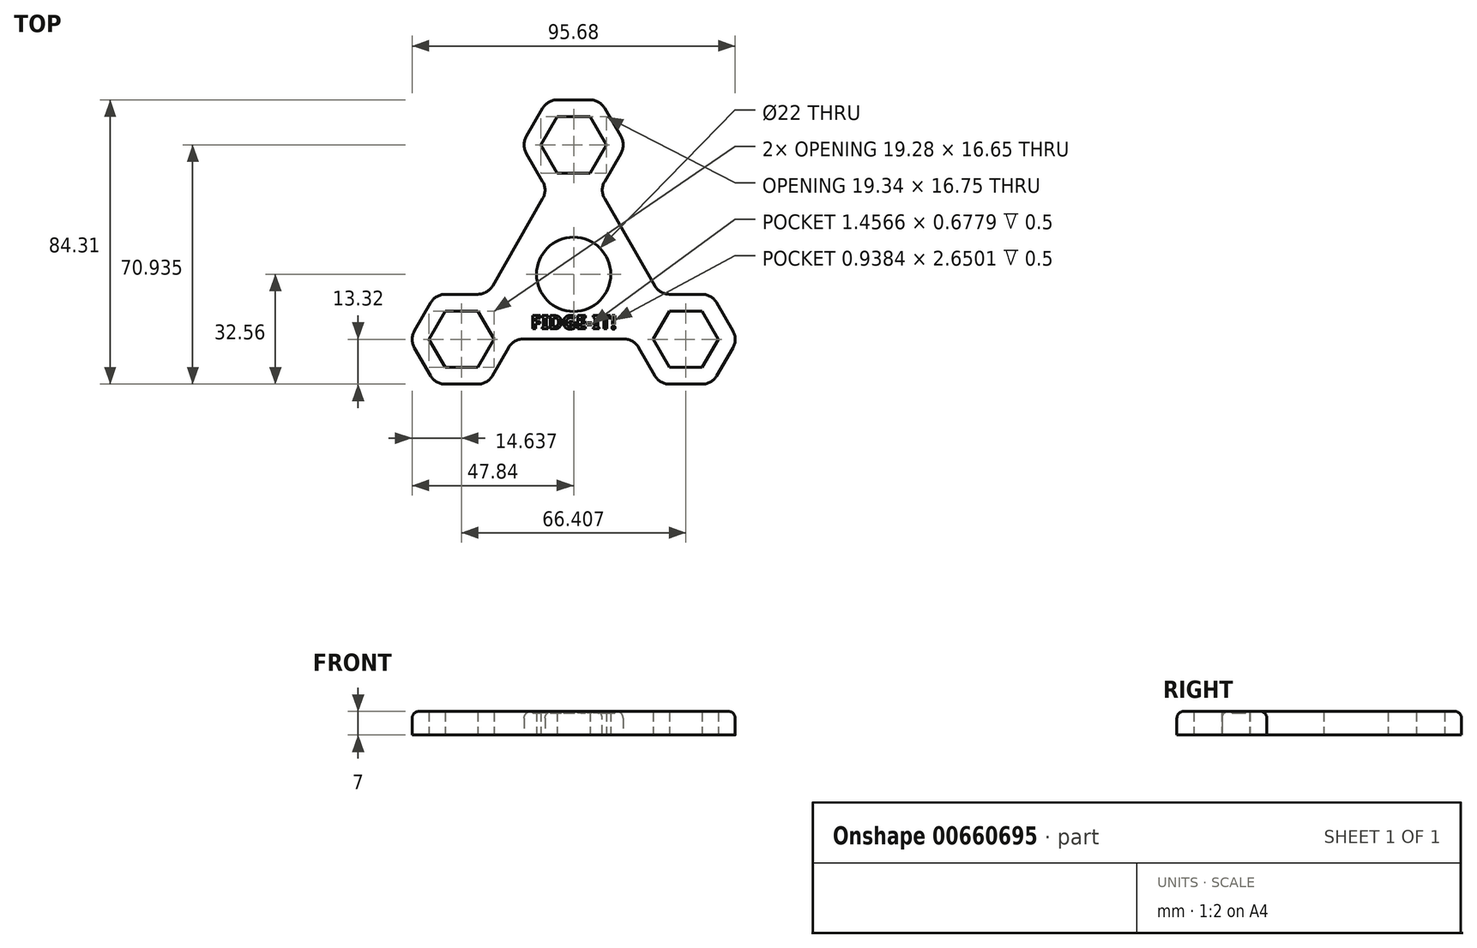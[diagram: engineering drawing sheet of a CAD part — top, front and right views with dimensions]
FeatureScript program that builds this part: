
annotation { "Feature Type Name" : "Feature", "Feature Type Description" : "" }
export const myFeature = defineFeature(function(context is Context, id is Id, definition is map)
    precondition{}
    {
        {
            var Q0;
            Q0=qCreatedBy(makeId("Top.planeOp"),FACE);
            var sketch = newSketch(context, id + "F0", { "sketchPlane" : qUnion([Q0])});
            skCircle(sketch, "E0", {"center": v(0, 0) * mm, "radius": 11 * mm});
            skLineSegment(sketch, "E1.0", {"start": v(4.84, 30) * mm, "end": v(-4.84, 30) * mm});
            skLineSegment(sketch, "E1.1", {"start": v(-4.84, 30) * mm, "end": v(-9.67, 38.38) * mm});
            skLineSegment(sketch, "E1.2", {"start": v(-9.67, 38.38) * mm, "end": v(-4.84, 46.75) * mm});
            skLineSegment(sketch, "E1.3", {"start": v(-4.84, 46.75) * mm, "end": v(4.84, 46.75) * mm});
            skLineSegment(sketch, "E1.4", {"start": v(4.84, 46.75) * mm, "end": v(9.67, 38.37) * mm});
            skLineSegment(sketch, "E1.5", {"start": v(9.67, 38.37) * mm, "end": v(4.84, 30) * mm});
            skPoint(sketch, "E1.0.midPoint", {"position": v(0, 30) * mm});
            skLineSegment(sketch, "E2.2.0", {"start": v(42.84, -19.3) * mm, "end": v(38.07, -27.56) * mm});
            skLineSegment(sketch, "E2.2.1", {"start": v(28.4, -27.56) * mm, "end": v(23.56, -19.19) * mm});
            skLineSegment(sketch, "E2.2.2", {"start": v(38.07, -27.56) * mm, "end": v(28.4, -27.56) * mm});
            skLineSegment(sketch, "E2.2.3", {"start": v(38, -10.92) * mm, "end": v(42.84, -19.3) * mm});
            skPoint(sketch, "E2.2.5", {"position": v(25.98, -15) * mm});
            skLineSegment(sketch, "E2.2.6", {"start": v(28.34, -10.92) * mm, "end": v(38, -10.92) * mm});
            skLineSegment(sketch, "E2.2.7", {"start": v(23.56, -19.19) * mm, "end": v(28.34, -10.92) * mm});
            skPoint(sketch, "E1.cCircle.center.orphan", {"position": v(0, 38.38) * mm});
            skLineSegment(sketch, "E3.0", {"start": v(-7.72, 25) * mm, "end": v(-15.44, 38.38) * mm});
            skLineSegment(sketch, "E3.1", {"start": v(-7.72, 51.75) * mm, "end": v(7.72, 51.75) * mm});
            skLineSegment(sketch, "E3.2", {"start": v(7.72, 51.75) * mm, "end": v(15.44, 38.37) * mm});
            skLineSegment(sketch, "E3.3", {"start": v(-15.44, 38.38) * mm, "end": v(-7.72, 51.75) * mm});
            skLineSegment(sketch, "E3.4", {"start": v(15.44, 38.37) * mm, "end": v(7.72, 25) * mm});
            skLineSegment(sketch, "E4.0", {"start": v(25.51, -32.56) * mm, "end": v(17.79, -19.19) * mm});
            skLineSegment(sketch, "E4.1", {"start": v(25.45, -5.92) * mm, "end": v(40.9, -5.92) * mm});
            skLineSegment(sketch, "E4.2", {"start": v(40.9, -5.92) * mm, "end": v(48.62, -19.3) * mm});
            skLineSegment(sketch, "E4.4", {"start": v(48.62, -19.3) * mm, "end": v(40.96, -32.56) * mm});
            skLineSegment(sketch, "E4.5", {"start": v(40.96, -32.56) * mm, "end": v(25.51, -32.56) * mm});
            skLineSegment(sketch, "E5.MirrorCS", {"start": v(-23.56, -19.19) * mm, "end": v(-28.34, -10.92) * mm});
            skPoint(sketch, "E6.MirrorP", {"position": v(-25.98, -15) * mm});
            skLineSegment(sketch, "E7.MirrorCS", {"start": v(-28.34, -10.92) * mm, "end": v(-38, -10.92) * mm});
            skLineSegment(sketch, "E8.MirrorCS", {"start": v(-40.96, -32.56) * mm, "end": v(-25.51, -32.56) * mm});
            skLineSegment(sketch, "E9.MirrorCS", {"start": v(-42.84, -19.3) * mm, "end": v(-38.07, -27.56) * mm});
            skLineSegment(sketch, "E10.MirrorCS", {"start": v(-38, -10.92) * mm, "end": v(-42.84, -19.3) * mm});
            skLineSegment(sketch, "E11.MirrorCS", {"start": v(-25.51, -32.56) * mm, "end": v(-17.79, -19.19) * mm});
            skLineSegment(sketch, "E12.MirrorCS", {"start": v(-48.62, -19.3) * mm, "end": v(-40.96, -32.56) * mm});
            skLineSegment(sketch, "E13.MirrorCS", {"start": v(-40.9, -5.92) * mm, "end": v(-48.62, -19.3) * mm});
            skLineSegment(sketch, "E14.MirrorCS", {"start": v(-28.4, -27.56) * mm, "end": v(-23.56, -19.19) * mm});
            skLineSegment(sketch, "E15.MirrorCS", {"start": v(-38.07, -27.56) * mm, "end": v(-28.4, -27.56) * mm});
            skLineSegment(sketch, "E16.MirrorCS", {"start": v(-25.45, -5.92) * mm, "end": v(-40.9, -5.92) * mm});
            skLineSegment(sketch, "E17", {"start": v(-7.72, 25) * mm, "end": v(-25.45, -5.92) * mm});
            skLineSegment(sketch, "E18", {"start": v(7.72, 25) * mm, "end": v(25.45, -5.92) * mm});
            skLineSegment(sketch, "E19", {"start": v(17.79, -19.19) * mm, "end": v(-17.79, -19.19) * mm});
            skSolve(sketch);
        }
        {
            var Q0;
            Q0=makeQuery(id+"F0.imprint","IMPRINT",FACE,{"disambiguationData":[TD([[makeQuery(id+"F0.imprint","IMPRINT",EDGE,{"derivedFrom":sQuery(id+"F0.wireOp",EDGE,"E1.0")}),1.0]])]});
            extrude(context, id + "F1", {"entities" : qUnion([Q0]), "depth" : 7 * mm, "offsetDistance" : 25 * mm});
        }
        {
            var Q0;
            Q0=makeQuery(id+"F1.opExtrude","SWEPT_EDGE",EDGE,{"disambiguationData":[OSD([sQuery(id+"F0.wireOp",EDGE,"E8.MirrorCS"),sQuery(id+"F0.wireOp",EDGE,"E11.MirrorCS")])]});
            var Q1;
            Q1=makeQuery(id+"F1.opExtrude","SWEPT_EDGE",EDGE,{"disambiguationData":[OSD([sQuery(id+"F0.wireOp",EDGE,"E8.MirrorCS"),sQuery(id+"F0.wireOp",EDGE,"E12.MirrorCS")])]});
            var Q2;
            Q2=makeQuery(id+"F1.opExtrude","SWEPT_EDGE",EDGE,{"disambiguationData":[OSD([sQuery(id+"F0.wireOp",EDGE,"E12.MirrorCS"),sQuery(id+"F0.wireOp",EDGE,"E13.MirrorCS")])]});
            var Q3;
            Q3=makeQuery(id+"F1.opExtrude","SWEPT_EDGE",EDGE,{"disambiguationData":[OSD([sQuery(id+"F0.wireOp",EDGE,"E13.MirrorCS"),sQuery(id+"F0.wireOp",EDGE,"E16.MirrorCS")])]});
            var Q4;
            Q4=makeQuery(id+"F1.opExtrude","SWEPT_EDGE",EDGE,{"disambiguationData":[OSD([sQuery(id+"F0.wireOp",EDGE,"E16.MirrorCS"),sQuery(id+"F0.wireOp",EDGE,"E17")])]});
            var Q5;
            Q5=makeQuery(id+"F1.opExtrude","SWEPT_EDGE",EDGE,{"disambiguationData":[OSD([sQuery(id+"F0.wireOp",EDGE,"E11.MirrorCS"),sQuery(id+"F0.wireOp",EDGE,"E19")])]});
            var Q6;
            Q6=makeQuery(id+"F1.opExtrude","SWEPT_EDGE",EDGE,{"disambiguationData":[OSD([sQuery(id+"F0.wireOp",EDGE,"E4.0"),sQuery(id+"F0.wireOp",EDGE,"E19")])]});
            var Q7;
            Q7=makeQuery(id+"F1.opExtrude","SWEPT_EDGE",EDGE,{"disambiguationData":[OSD([sQuery(id+"F0.wireOp",EDGE,"E4.0"),sQuery(id+"F0.wireOp",EDGE,"E4.5")])]});
            var Q8;
            Q8=makeQuery(id+"F1.opExtrude","SWEPT_EDGE",EDGE,{"disambiguationData":[OSD([sQuery(id+"F0.wireOp",EDGE,"E4.4"),sQuery(id+"F0.wireOp",EDGE,"E4.5")])]});
            var Q9;
            Q9=makeQuery(id+"F1.opExtrude","SWEPT_EDGE",EDGE,{"disambiguationData":[OSD([sQuery(id+"F0.wireOp",EDGE,"E4.2"),sQuery(id+"F0.wireOp",EDGE,"E4.4")])]});
            var Q10;
            Q10=makeQuery(id+"F1.opExtrude","SWEPT_EDGE",EDGE,{"disambiguationData":[OSD([sQuery(id+"F0.wireOp",EDGE,"E4.1"),sQuery(id+"F0.wireOp",EDGE,"E4.2")])]});
            var Q11;
            Q11=makeQuery(id+"F1.opExtrude","SWEPT_EDGE",EDGE,{"disambiguationData":[OSD([sQuery(id+"F0.wireOp",EDGE,"E4.1"),sQuery(id+"F0.wireOp",EDGE,"E18")])]});
            var Q12;
            Q12=makeQuery(id+"F1.opExtrude","SWEPT_EDGE",EDGE,{"disambiguationData":[OSD([sQuery(id+"F0.wireOp",EDGE,"E3.4"),sQuery(id+"F0.wireOp",EDGE,"E18")])]});
            var Q13;
            Q13=makeQuery(id+"F1.opExtrude","SWEPT_EDGE",EDGE,{"disambiguationData":[OSD([sQuery(id+"F0.wireOp",EDGE,"E3.2"),sQuery(id+"F0.wireOp",EDGE,"E3.4")])]});
            var Q14;
            Q14=makeQuery(id+"F1.opExtrude","SWEPT_EDGE",EDGE,{"disambiguationData":[OSD([sQuery(id+"F0.wireOp",EDGE,"E3.1"),sQuery(id+"F0.wireOp",EDGE,"E3.2")])]});
            var Q15;
            Q15=makeQuery(id+"F1.opExtrude","SWEPT_EDGE",EDGE,{"disambiguationData":[OSD([sQuery(id+"F0.wireOp",EDGE,"E3.1"),sQuery(id+"F0.wireOp",EDGE,"E3.3")])]});
            var Q16;
            Q16=makeQuery(id+"F1.opExtrude","SWEPT_EDGE",EDGE,{"disambiguationData":[OSD([sQuery(id+"F0.wireOp",EDGE,"E3.0"),sQuery(id+"F0.wireOp",EDGE,"E3.3")])]});
            var Q17;
            Q17=makeQuery(id+"F1.opExtrude","SWEPT_EDGE",EDGE,{"disambiguationData":[OSD([sQuery(id+"F0.wireOp",EDGE,"E3.0"),sQuery(id+"F0.wireOp",EDGE,"E17")])]});
            fillet(context, id + "F2", {"entities" : qUnion([Q0, Q1, Q2, Q3, Q4, Q5, Q6, Q7, Q8, Q9, Q10, Q11, Q12, Q13, Q14, Q15, Q16, Q17]), "radius" : 5 * mm, "tangentPropagation" : true, "allowEdgeOverflow" : false});
        }
        {
            var Q0;
            Q0=makeQuery(id+"F1.opExtrude","CAP_EDGE",EDGE,{"disambiguationData":[OSD([sQuery(id+"F0.wireOp",EDGE,"E19")])],"isStart":false});
            fillet(context, id + "F3", {"entities" : qUnion([Q0]), "radius" : 2 * mm, "tangentPropagation" : true, "allowEdgeOverflow" : false});
        }
        {
            var Q0;
            Q0=makeQuery(id+"F1.opExtrude","CAP_FACE",FACE,{"disambiguationData":[OSD([sQuery(id+"F0.wireOp",EDGE,"E1.0"),sQuery(id+"F0.wireOp",EDGE,"E1.1"),sQuery(id+"F0.wireOp",EDGE,"E1.2"),sQuery(id+"F0.wireOp",EDGE,"E1.3"),sQuery(id+"F0.wireOp",EDGE,"E1.4"),sQuery(id+"F0.wireOp",EDGE,"E1.5"),sQuery(id+"F0.wireOp",EDGE,"E2.2.0"),sQuery(id+"F0.wireOp",EDGE,"E2.2.1"),sQuery(id+"F0.wireOp",EDGE,"E2.2.2"),sQuery(id+"F0.wireOp",EDGE,"E2.2.3"),sQuery(id+"F0.wireOp",EDGE,"E2.2.6"),sQuery(id+"F0.wireOp",EDGE,"E2.2.7"),sQuery(id+"F0.wireOp",EDGE,"E0"),sQuery(id+"F0.wireOp",EDGE,"E3.0"),sQuery(id+"F0.wireOp",EDGE,"E3.1"),sQuery(id+"F0.wireOp",EDGE,"E3.2"),sQuery(id+"F0.wireOp",EDGE,"E3.3"),sQuery(id+"F0.wireOp",EDGE,"E3.4"),sQuery(id+"F0.wireOp",EDGE,"E4.0"),sQuery(id+"F0.wireOp",EDGE,"E4.1"),sQuery(id+"F0.wireOp",EDGE,"E4.2"),sQuery(id+"F0.wireOp",EDGE,"E4.4"),sQuery(id+"F0.wireOp",EDGE,"E4.5"),sQuery(id+"F0.wireOp",EDGE,"E5.MirrorCS"),sQuery(id+"F0.wireOp",EDGE,"E7.MirrorCS"),sQuery(id+"F0.wireOp",EDGE,"E8.MirrorCS"),sQuery(id+"F0.wireOp",EDGE,"E9.MirrorCS"),sQuery(id+"F0.wireOp",EDGE,"E10.MirrorCS"),sQuery(id+"F0.wireOp",EDGE,"E11.MirrorCS"),sQuery(id+"F0.wireOp",EDGE,"E12.MirrorCS"),sQuery(id+"F0.wireOp",EDGE,"E13.MirrorCS"),sQuery(id+"F0.wireOp",EDGE,"E14.MirrorCS"),sQuery(id+"F0.wireOp",EDGE,"E15.MirrorCS"),sQuery(id+"F0.wireOp",EDGE,"E16.MirrorCS"),sQuery(id+"F0.wireOp",EDGE,"E17"),sQuery(id+"F0.wireOp",EDGE,"E18"),sQuery(id+"F0.wireOp",EDGE,"E19")])],"isStart":false});
            var sketch = newSketch(context, id + "F4", { "sketchPlane" : qUnion([Q0])});
            skText(sketch, "E20", { "text": "FIDGE-IT!", "fontName": "NotoSans-Bold.ttf"});
            const initialGuessF4  = {"E20": [-0.01263, -0.01619, 1, 0, 0.004]};
            skSetInitialGuess(sketch, initialGuessF4);
            skSolve(sketch);
        }
        {
            var Q0;
            Q0 = qSketchRegion(id + "F4", true);
            extrude(context, id + "F5", {"entities" : qUnion([Q0]), "operationType" : NewBodyOperationType.REMOVE, "oppositeDirection" : true, "depth" : 0.5 * mm, "offsetDistance" : 25 * mm});
        }
    });
